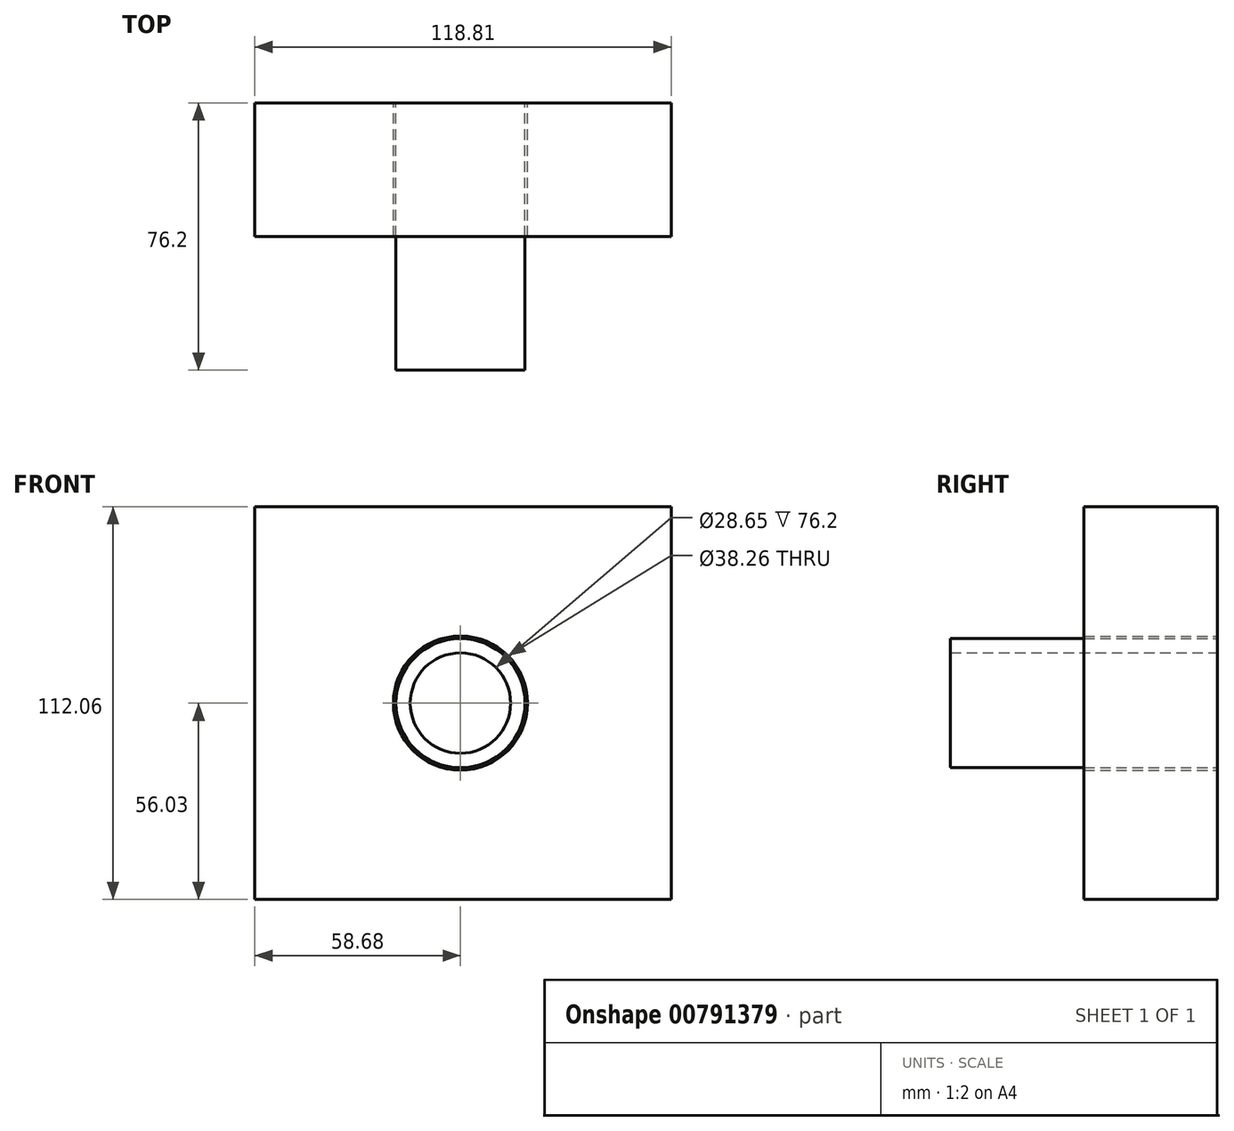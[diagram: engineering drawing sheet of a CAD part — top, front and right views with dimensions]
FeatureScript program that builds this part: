
annotation { "Feature Type Name" : "Feature", "Feature Type Description" : "" }
export const myFeature = defineFeature(function(context is Context, id is Id, definition is map)
    precondition{}
    {
        {
            var Q0;
            Q0=qCreatedBy(makeId("Front.planeOp"),FACE);
            var sketch = newSketch(context, id + "F0", { "sketchPlane" : qUnion([Q0])});
            skLineSegment(sketch, "E0.bottom", {"start": v(-58.68, 56.03) * mm, "end": v(60.13, 56.03) * mm});
            skLineSegment(sketch, "E0.top", {"start": v(-58.68, -56.03) * mm, "end": v(60.13, -56.03) * mm});
            skLineSegment(sketch, "E0.left", {"start": v(-58.68, 56.03) * mm, "end": v(-58.68, -56.03) * mm});
            skLineSegment(sketch, "E0.right", {"start": v(60.13, 56.03) * mm, "end": v(60.13, -56.03) * mm});
            skCircle(sketch, "E1", {"center": v(0, 0) * mm, "radius": 25.6 * mm});
            skCircle(sketch, "E2", {"center": v(0, 0) * mm, "radius": 19.13 * mm});
            skSolve(sketch);
        }
        {
            var Q0;
            Q0=makeQuery(id+"F0.imprint","IMPRINT",FACE,{"disambiguationData":[TD([[makeQuery(id+"F0.imprint","IMPRINT",EDGE,{"derivedFrom":sQuery(id+"F0.wireOp",EDGE,"E1")}),1.0]])]});
            var Q1;
            Q1=makeQuery(id+"F0.imprint","IMPRINT",FACE,{"disambiguationData":[TD([[makeQuery(id+"F0.imprint","IMPRINT",EDGE,{"derivedFrom":sQuery(id+"F0.wireOp",EDGE,"E0.bottom")}),-1.0]])]});
            extrude(context, id + "F1", {"entities" : qUnion([Q0, Q1]), "depth" : 38.1 * mm, "offsetDistance" : 25.4 * mm});
        }
        {
            var Q0;
            Q0=makeQuery(id+"F1.opExtrude","CAP_FACE",FACE,{"disambiguationData":[OSD([sQuery(id+"F0.wireOp",EDGE,"E0.bottom"),sQuery(id+"F0.wireOp",EDGE,"E0.top"),sQuery(id+"F0.wireOp",EDGE,"E0.left"),sQuery(id+"F0.wireOp",EDGE,"E0.right"),sQuery(id+"F0.wireOp",EDGE,"E2")])],"isStart":true});
            var sketch = newSketch(context, id + "F2", { "sketchPlane" : qUnion([Q0])});
            skCircle(sketch, "E3", {"center": v(0, 0) * mm, "radius": 18.44 * mm});
            skCircle(sketch, "E4", {"center": v(0, 0) * mm, "radius": 14.33 * mm});
            skSolve(sketch);
        }
        {
            var Q0;
            Q0=makeQuery(id+"F2.imprint","IMPRINT",FACE,{"disambiguationData":[TD([[makeQuery(id+"F2.imprint","IMPRINT",EDGE,{"derivedFrom":sQuery(id+"F2.wireOp",EDGE,"E3")}),1.0]])]});
            extrude(context, id + "F3", {"entities" : qUnion([Q0]), "oppositeDirection" : true, "depth" : 76.2 * mm, "offsetDistance" : 25.4 * mm});
        }
    });
